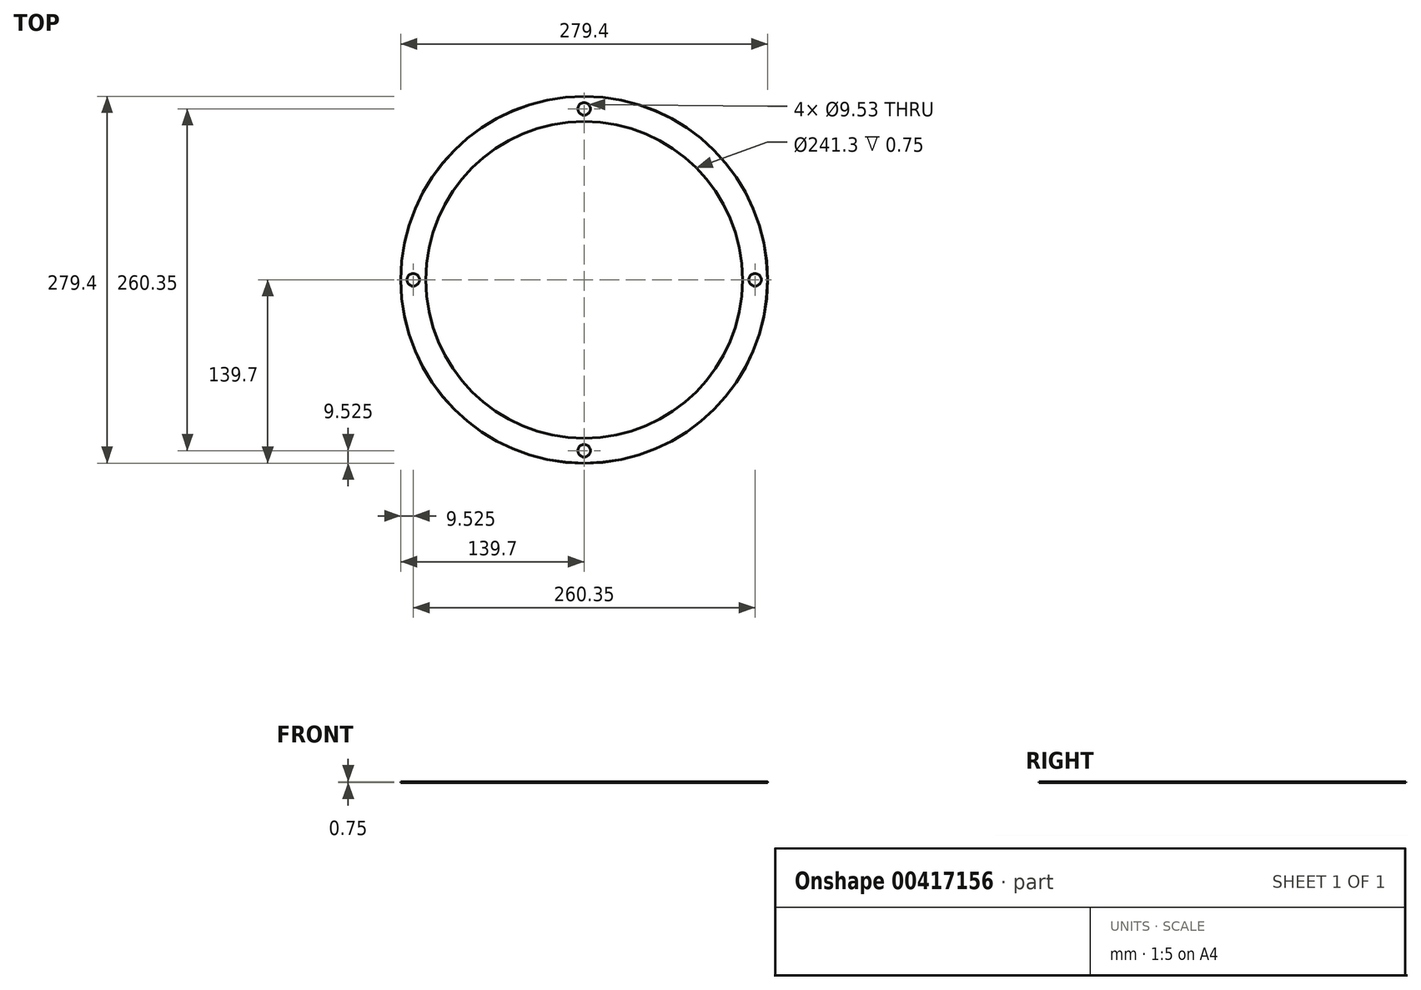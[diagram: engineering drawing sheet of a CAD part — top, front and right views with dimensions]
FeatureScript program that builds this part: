
annotation { "Feature Type Name" : "Feature", "Feature Type Description" : "" }
export const myFeature = defineFeature(function(context is Context, id is Id, definition is map)
    precondition{}
    {
        {
            assignVariable(context, id + "F0", {"name" : "BaseThickness", "anyValue" : 0.75});
        }
        {
            assignVariable(context, id + "F1", {"name" : "OuterChamfer", "anyValue" : 0.06});
        }
        {
            var Q0;
            Q0=qCreatedBy(makeId("Top.planeOp"),FACE);
            var sketch = newSketch(context, id + "F2", { "sketchPlane" : qUnion([Q0])});
            skCircle(sketch, "E0", {"center": v(0, 0) * mm, "radius": 139.7 * mm});
            skSolve(sketch);
        }
        {
            var Q0;
            Q0=qSketchRegion(id+"F2",true);
            extrude(context, id + "F3", {"entities" : qUnion([Q0]), "depth" : (getVariable(context, 'BaseThickness')) * mm});
        }
        {
            var Q0;
            Q0=makeQuery(id+"F3.opExtrude","CAP_EDGE",EDGE,{"disambiguationData":[OSD([sQuery(id+"F2.wireOp",EDGE,"E0")])],"isStart":false});
            var Q1;
            Q1=makeQuery(id+"F3.opExtrude","CAP_EDGE",EDGE,{"disambiguationData":[OSD([sQuery(id+"F2.wireOp",EDGE,"E0")])],"isStart":true});
            chamfer(context, id + "F4", {"entities" : qUnion([Q0, Q1]), "width" : (getVariable(context, 'OuterChamfer')) * mm, "tangentPropagation" : true});
        }
        {
            var Q0;
            Q0=makeQuery(id+"F3.opExtrude","CAP_FACE",FACE,{"disambiguationData":[OSD([sQuery(id+"F2.wireOp",EDGE,"E0")])],"isStart":true});
            var sketch = newSketch(context, id + "F5", { "sketchPlane" : qUnion([Q0])});
            skCircle(sketch, "E1", {"center": v(0, 0) * mm, "radius": 120.65 * mm});
            skSolve(sketch);
        }
        {
            var Q0;
            Q0=makeQuery(id+"F5.imprint","IMPRINT",FACE,{"disambiguationData":[TD([[makeQuery(id+"F5.imprint","IMPRINT",EDGE,{"derivedFrom":sQuery(id+"F5.wireOp",EDGE,"E1")}),1.0]])]});
            extrude(context, id + "F6", {"entities" : qUnion([Q0]), "operationType" : NewBodyOperationType.REMOVE, "endBound" : BoundingType.THROUGH_ALL, "oppositeDirection" : true, "depth" : 25.4 * mm});
        }
        {
            var Q0;
            Q0=makeQuery(id+"F3.opExtrude","CAP_FACE",FACE,{"disambiguationData":[OSD([sQuery(id+"F2.wireOp",EDGE,"E0")])],"isStart":false});
            var sketch = newSketch(context, id + "F7", { "sketchPlane" : qUnion([Q0])});
            skCircle(sketch, "E2", {"center": v(0, 130.18) * mm, "radius": 0.8 * mm});
            skCircle(sketch, "E3.1.0", {"center": v(130.18, 0) * mm, "radius": 0.8 * mm});
            skCircle(sketch, "E3.2.0", {"center": v(0, -130.18) * mm, "radius": 0.8 * mm});
            skCircle(sketch, "E3.3.0", {"center": v(-130.18, 0) * mm, "radius": 0.8 * mm});
            skPoint(sketch, "E3.center", {"position": v(0, 0) * mm});
            skLineSegment(sketch, "E3.anchor1", {"start": v(0, 0) * mm, "end": v(0, 130.18) * mm, "construction": true});
            skLineSegment(sketch, "E3.anchor2", {"start": v(0, 0) * mm, "end": v(-130.18, 0) * mm, "construction": true});
            skSolve(sketch);
        }
        {
            var Q0;
            Q0=makeQuery(id+"F7.imprint","IMPRINT",FACE,{"disambiguationData":[TD([[makeQuery(id+"F7.imprint","IMPRINT",EDGE,{"derivedFrom":sQuery(id+"F7.wireOp",EDGE,"E2")}),1.0]])]});
            var Q1;
            Q1=makeQuery(id+"F7.imprint","IMPRINT",FACE,{"disambiguationData":[TD([[makeQuery(id+"F7.imprint","IMPRINT",EDGE,{"derivedFrom":sQuery(id+"F7.wireOp",EDGE,"E3.1.0")}),1.0]])]});
            var Q2;
            Q2=makeQuery(id+"F7.imprint","IMPRINT",FACE,{"disambiguationData":[TD([[makeQuery(id+"F7.imprint","IMPRINT",EDGE,{"derivedFrom":sQuery(id+"F7.wireOp",EDGE,"E3.2.0")}),1.0]])]});
            var Q3;
            Q3=makeQuery(id+"F7.imprint","IMPRINT",FACE,{"disambiguationData":[TD([[makeQuery(id+"F7.imprint","IMPRINT",EDGE,{"derivedFrom":sQuery(id+"F7.wireOp",EDGE,"E3.3.0")}),1.0]])]});
            extrude(context, id + "F8", {"entities" : qUnion([Q0, Q1, Q2, Q3]), "operationType" : NewBodyOperationType.REMOVE, "endBound" : BoundingType.THROUGH_ALL, "oppositeDirection" : true, "depth" : 25.4 * mm});
        }
        {
            var Q0;
            Q0=makeQuery(id+"F3.opExtrude","CAP_FACE",FACE,{"disambiguationData":[OSD([sQuery(id+"F2.wireOp",EDGE,"E0")])],"isStart":false});
            var sketch = newSketch(context, id + "F9", { "sketchPlane" : qUnion([Q0])});
            skCircle(sketch, "E4", {"center": v(0, 130.18) * mm, "radius": 4.76 * mm});
            skCircle(sketch, "E5.1.0", {"center": v(-130.18, 0) * mm, "radius": 4.76 * mm});
            skCircle(sketch, "E5.2.0", {"center": v(0, -130.18) * mm, "radius": 4.76 * mm});
            skCircle(sketch, "E5.3.0", {"center": v(130.18, 0) * mm, "radius": 4.76 * mm});
            skPoint(sketch, "E5.center", {"position": v(0, 0) * mm});
            skSolve(sketch);
        }
        {
            var Q0;
            Q0=makeQuery(id+"F9.imprint","IMPRINT",FACE,{"disambiguationData":[TD([[makeQuery(id+"F9.imprint","IMPRINT",EDGE,{"derivedFrom":sQuery(id+"F9.wireOp",EDGE,"E4")}),1.0]])]});
            var Q1;
            Q1=makeQuery(id+"F9.imprint","IMPRINT",FACE,{"disambiguationData":[TD([[makeQuery(id+"F9.imprint","IMPRINT",EDGE,{"derivedFrom":sQuery(id+"F9.wireOp",EDGE,"E5.3.0")}),1.0]])]});
            var Q2;
            Q2=makeQuery(id+"F9.imprint","IMPRINT",FACE,{"disambiguationData":[TD([[makeQuery(id+"F9.imprint","IMPRINT",EDGE,{"derivedFrom":sQuery(id+"F9.wireOp",EDGE,"E5.1.0")}),1.0]])]});
            var Q3;
            Q3=makeQuery(id+"F9.imprint","IMPRINT",FACE,{"disambiguationData":[TD([[makeQuery(id+"F9.imprint","IMPRINT",EDGE,{"derivedFrom":sQuery(id+"F9.wireOp",EDGE,"E5.2.0")}),1.0]])]});
            extrude(context, id + "F10", {"entities" : qUnion([Q0, Q1, Q2, Q3]), "operationType" : NewBodyOperationType.REMOVE, "oppositeDirection" : true, "depth" : 15.88 * mm});
        }
    });
